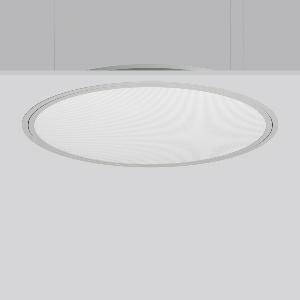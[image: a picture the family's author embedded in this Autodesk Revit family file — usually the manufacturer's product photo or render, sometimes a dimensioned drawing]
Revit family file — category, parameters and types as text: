
# Revit family: triona_round_e_312299_004_12_b30d
name_source: partatom
category: Lighting Fixtures
units: mm (PartAtom-declared; Revit-internal decimal feet)

## family parameters
Cut with Voids When Loaded = No
Host = Face
Light Source = No
Part Type = Normal
Room Calculation Point = No
Round Connector Dimension = Use Diameter
Shared = No

## types (1)
- TRIONA round E (1 x LED Modul 830, 8050 lm, 3000)
    Apparent Load = 66 VA
    CIE Flux Codes = 59 87 97 100 100
    Color Rendering = 80
    Color Temperature = 3000
    Default Elevation = 1800 mm
    Description = Series: TRIONA round
Decorative round LED recessed surface luminaire. Cover made of sheet steel, powder-coated. Frame made of aluminium, powder-coated. Recessed ring: aluminium extrusion profile, powder coated. Light emission through a diffuser in plastic, opal/prismatic. Lightguide and diffuser made of non-yellowing plastic (PMMA). Lateral light emission (RZB SIDELITE technology) for above-average homogeneous light distribution. Suitable for installation in cavity ceilings. Tool-free mounting system thanks to the rocker arm mechanism (patent pending). Electronic ballast included. Very easy installation thanks to Plug+Play connection. 
Colour: silver, matt (approx. RAL 9006)
Diameter: 889 mm
Height: 2 mm
Cut-out diameter: 866 mm
Recess height: 100 mm
Luminaire: recess height: 89 mm
Lamp: LED
Socket: without socket
Colour temperature: 3000K
Colour rendering index (CRI): 80
System power: 66 W
Rated luminous flux: 8050 lm
Luminous efficiency: 122 lm/W
Control gear: Converter, dimmable, DALI
Protection class: I
Type of protection: IP 40
    Height = 0 mm  [stored 0 ft]
    Lamp = 1 x LED Modul 830
    Lamp Light Flux = 8050 lm
    Lamp count = 1
    Length = 889 mm
    Lifetime = 50000 h
    Luminous efficacy = 122 lm/W
    Manufacturer = RZB
    ModVariant = No
    Model = 312299.004.12
    Mounting Place = Ceiling
    Mounting Type = Recessed
    Number of Poles = 1
    OnlyDefault = Yes
    Power Factor = 1
    Product Name = TRIONA round E
    Product group = Recessed modular luminaires
    ProductGroupID = 406
    Protection Class = Protection class I
    Protection Degree = IP 20
    RLX_Detail_Level = 1
    RLX_Emergency_Light_Flux = 0 lm
    RLX_Emergency_Type = 0
    RLX_Emergency_Type_DB = No
    RlxData = <blob elided: 41829 chars, md5=ad9d6d8d>
    Socket = socket
    Standby Power = 0 W
    System Light Flux = 8050 lm
    System Power = 66 W
    Type Comments = Product without accessories
    Type Image = 312299.004.12.jpg
    URL = http://relux.com
    VarID = ---
    Voltage = 230 V
    Voltage Range = 220-240 V
    Weight = 0.00 kg
    Width = 0 mm  [stored 0 ft]

note: [stored X ft] marks values corroborated as IEEE doubles in the binary element streams (Revit-internal decimal feet)

## geometry (parser evidence)
native form markers: Blend x4, Sweep x8
no freeform markers — native parametric forms only
